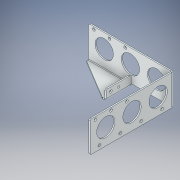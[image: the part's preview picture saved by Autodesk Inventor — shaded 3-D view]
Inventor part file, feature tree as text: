
AUTODESK INVENTOR PART (.ipt)
format: ipt  version: 2019 (Build 230136000, 136)  size: 165,376 bytes
history: native  units: in
note: dims shown in document units (in); Inventor stores cm internally (conversion verified against a paired STEP export)
features: fillet x1
ambient origin geometry x8: Origin, YZ Plane, XZ Plane, XY Plane, X Axis, Y Axis, Z Axis, Center Point
bodies: Solid1 (feature_tree)
feature tree (1):
  fillet  "Fillet1"  [1 undecoded]
note: 1 required parameter value undecoded (feature->parameter linkage not recoverable at this tier; creation-order binding heuristic only, values carry confidence <= 0.55)
